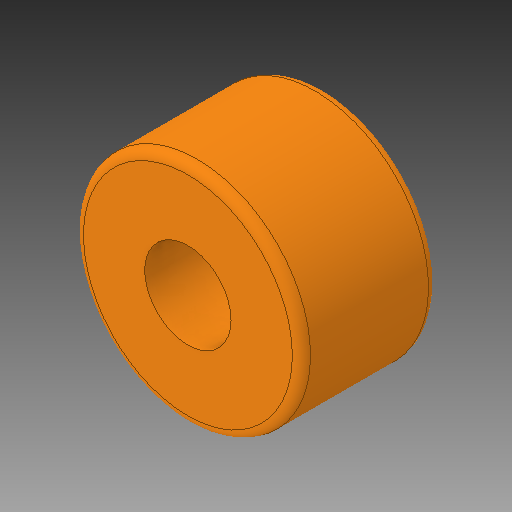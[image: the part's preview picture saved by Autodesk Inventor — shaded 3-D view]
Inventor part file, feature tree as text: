
AUTODESK INVENTOR PART (.ipt)
format: ipt  version: 2019 (Build 230136000, 136)  size: 123,904 bytes
history: native  units: mm
features: other x1, extrude x1, fillet x1, sketch x1
ambient origin geometry x8: Origin, YZ Plane, XZ Plane, XY Plane, X Axis, Y Axis, Z Axis, Center Point
bodies: Body1 (feature_tree)
feature tree (4):
  other  "Твердое тело1"
  extrude  "Выдавливание1"  Depth=25.0mm
  fillet  "Сопряжение1"  Radius=9.5mm
  sketch  "Эскиз1"
